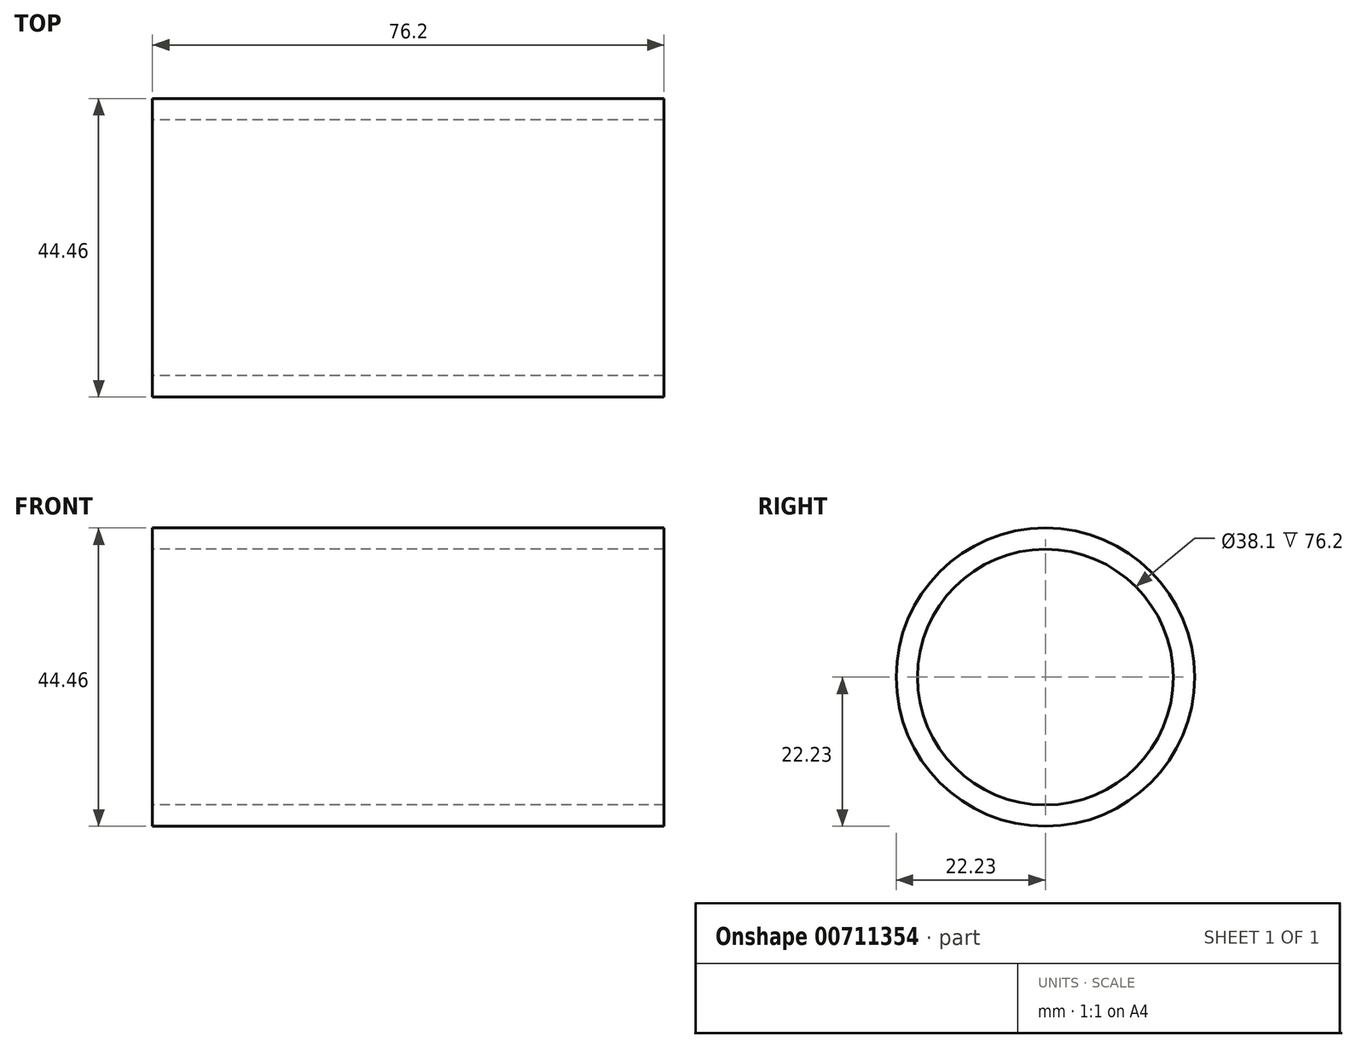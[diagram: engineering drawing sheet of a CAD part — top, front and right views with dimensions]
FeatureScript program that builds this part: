
annotation { "Feature Type Name" : "Feature", "Feature Type Description" : "" }
export const myFeature = defineFeature(function(context is Context, id is Id, definition is map)
    precondition{}
    {
        {
            var Q0;
            Q0=qCreatedBy(makeId("Right.planeOp"),FACE);
            var sketch = newSketch(context, id + "F0", { "sketchPlane" : qUnion([Q0])});
            skCircle(sketch, "E0", {"center": v(0, 0) * mm, "radius": 19.05 * mm});
            skCircle(sketch, "E1", {"center": v(0, 0) * mm, "radius": 22.23 * mm});
            skSolve(sketch);
        }
        {
            var Q0;
            Q0=makeQuery(id+"F0.imprint","IMPRINT",FACE,{"disambiguationData":[TD([[makeQuery(id+"F0.imprint","IMPRINT",EDGE,{"derivedFrom":sQuery(id+"F0.wireOp",EDGE,"E0")}),-1.0]])]});
            extrude(context, id + "F1", {"entities" : qUnion([Q0]), "endBound" : BoundingType.SYMMETRIC, "depth" : 76.2 * mm, "offsetDistance" : 25.4 * mm});
        }
    });
